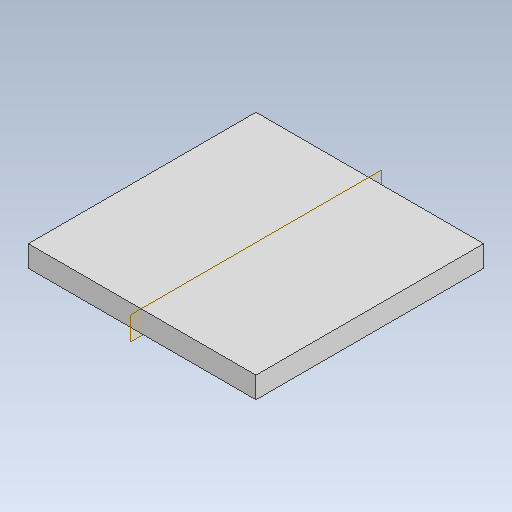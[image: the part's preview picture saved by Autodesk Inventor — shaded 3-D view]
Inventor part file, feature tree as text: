
AUTODESK INVENTOR PART (.ipt)
format: ipt  version: 2021 (Build 250183000, 183)  size: 91,136 bytes
history: native  units: in
note: dims shown in document units (in); Inventor stores cm internally (conversion verified against a paired STEP export)
features: extrude x1, sketch x1
ambient origin geometry x8: Origin, YZ Plane, XZ Plane, XY Plane, X Axis, Y Axis, Z Axis, Center Point
bodies: Solid1 (feature_tree)
feature tree (2):
  extrude  "Extrusion1"  Depth=8.0in
  sketch  "Sketch1"  dims[d0=8.0in d1=8.0in d2=0.75in d3=0.0in]
